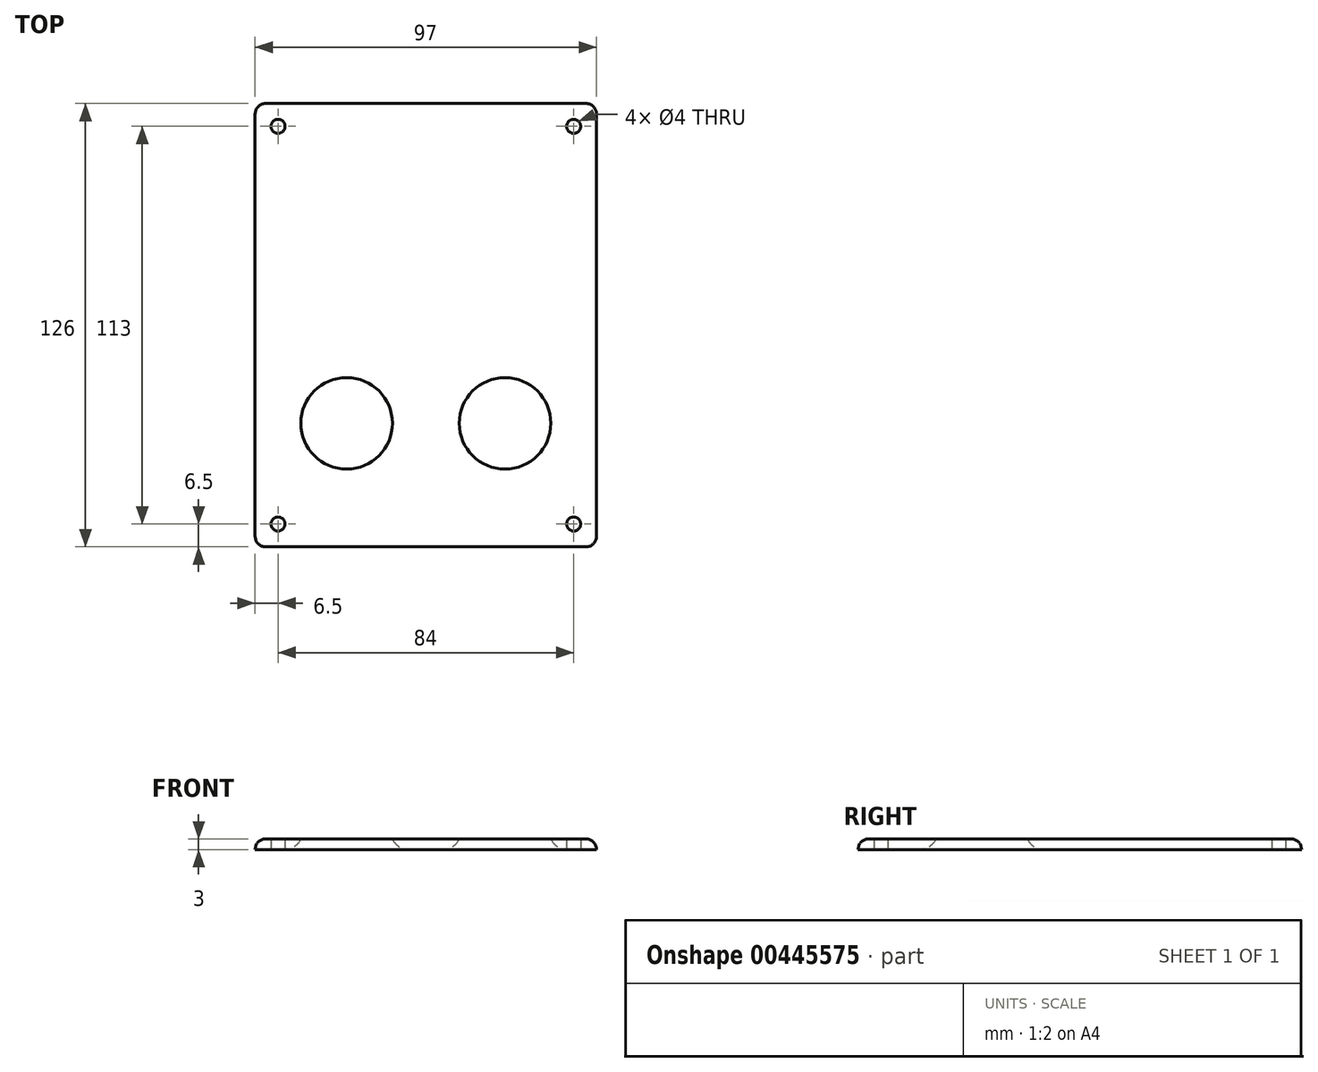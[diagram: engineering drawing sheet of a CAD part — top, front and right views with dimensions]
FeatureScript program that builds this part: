
annotation { "Feature Type Name" : "Feature", "Feature Type Description" : "" }
export const myFeature = defineFeature(function(context is Context, id is Id, definition is map)
    precondition{}
    {
        {
            var Q0;
            Q0=qCreatedBy(makeId("Top.planeOp"),FACE);
            var sketch = newSketch(context, id + "F0", { "sketchPlane" : qUnion([Q0])});
            skLineSegment(sketch, "E0.bottom", {"start": v(48.5, 63) * mm, "end": v(-48.5, 63) * mm});
            skLineSegment(sketch, "E0.top", {"start": v(48.5, -63) * mm, "end": v(-48.5, -63) * mm});
            skLineSegment(sketch, "E0.left", {"start": v(48.5, 63) * mm, "end": v(48.5, -63) * mm});
            skLineSegment(sketch, "E0.right", {"start": v(-48.5, 63) * mm, "end": v(-48.5, -63) * mm});
            skPoint(sketch, "E0.middle", {"position": v(0, 0) * mm});
            skLineSegment(sketch, "E1", {"start": v(-48.5, -27.89) * mm, "end": v(48.5, -27.88) * mm, "construction": true});
            skCircle(sketch, "E2", {"center": v(-22.5, -27.88) * mm, "radius": 13 * mm});
            skCircle(sketch, "E3", {"center": v(22.5, -27.88) * mm, "radius": 13 * mm});
            skLineSegment(sketch, "E4", {"start": v(-42, -63) * mm, "end": v(-42, 63) * mm, "construction": true});
            skLineSegment(sketch, "E5", {"start": v(0, -63) * mm, "end": v(0, 63) * mm, "construction": true});
            skLineSegment(sketch, "E6", {"start": v(-48.5, 56.5) * mm, "end": v(48.5, 56.5) * mm, "construction": true});
            skLineSegment(sketch, "E7", {"start": v(-48.5, 0) * mm, "end": v(48.5, 0) * mm, "construction": true});
            skCircle(sketch, "E8", {"center": v(-42, 56.5) * mm, "radius": 2 * mm});
            skCircle(sketch, "E9.MirrorC", {"center": v(42, 56.5) * mm, "radius": 2 * mm});
            skLineSegment(sketch, "E10.MirrorCS", {"start": v(48.5, 0) * mm, "end": v(-48.5, 0) * mm, "construction": true});
            skCircle(sketch, "E11.MirrorC", {"center": v(42, -56.5) * mm, "radius": 2 * mm});
            skCircle(sketch, "E12.MirrorC", {"center": v(-42, -56.5) * mm, "radius": 2 * mm});
            skLineSegment(sketch, "E13", {"start": v(-22.5, -63) * mm, "end": v(-22.5, 21.5) * mm, "construction": true});
            skLineSegment(sketch, "E14", {"start": v(22.5, -63) * mm, "end": v(22.5, 14.03) * mm, "construction": true});
            skSolve(sketch);
        }
        {
            var Q0;
            Q0=makeQuery(id+"F0.imprint","IMPRINT",FACE,{"disambiguationData":[TD([[makeQuery(id+"F0.imprint","IMPRINT",EDGE,{"derivedFrom":sQuery(id+"F0.wireOp",EDGE,"E0.bottom")}),1.0]])]});
            extrude(context, id + "F1", {"entities" : qUnion([Q0]), "depth" : 3 * mm});
        }
        {
            var Q0;
            Q0=makeQuery(id+"F1.opExtrude","CAP_EDGE",EDGE,{"disambiguationData":[OSD([sQuery(id+"F0.wireOp",EDGE,"E2")])],"isStart":true});
            fillet(context, id + "F2", {"entities" : qUnion([Q0]), "radius" : 5 * mm, "tangentPropagation" : true, "allowEdgeOverflow" : false});
        }
        {
            var Q0;
            Q0=makeQuery(id+"F1.opExtrude","CAP_EDGE",EDGE,{"disambiguationData":[OSD([sQuery(id+"F0.wireOp",EDGE,"E3")])],"isStart":true});
            fillet(context, id + "F3", {"entities" : qUnion([Q0]), "radius" : 5 * mm, "tangentPropagation" : true, "allowEdgeOverflow" : false});
        }
        {
            var Q0;
            Q0=makeQuery(id+"F1.opExtrude","SWEPT_EDGE",EDGE,{"disambiguationData":[OSD([sQuery(id+"F0.wireOp",EDGE,"E0.top"),sQuery(id+"F0.wireOp",EDGE,"E0.left")])]});
            var Q1;
            Q1=makeQuery(id+"F1.opExtrude","SWEPT_EDGE",EDGE,{"disambiguationData":[OSD([sQuery(id+"F0.wireOp",EDGE,"E0.top"),sQuery(id+"F0.wireOp",EDGE,"E0.right")])]});
            fillet(context, id + "F4", {"entities" : qUnion([Q0, Q1]), "radius" : 3 * mm, "tangentPropagation" : true, "allowEdgeOverflow" : false});
        }
        {
            var Q0;
            Q0=makeQuery(id+"F1.opExtrude","SWEPT_EDGE",EDGE,{"disambiguationData":[OSD([sQuery(id+"F0.wireOp",EDGE,"E0.bottom"),sQuery(id+"F0.wireOp",EDGE,"E0.left")])]});
            var Q1;
            Q1=makeQuery(id+"F1.opExtrude","SWEPT_EDGE",EDGE,{"disambiguationData":[OSD([sQuery(id+"F0.wireOp",EDGE,"E0.bottom"),sQuery(id+"F0.wireOp",EDGE,"E0.right")])]});
            fillet(context, id + "F5", {"entities" : qUnion([Q0, Q1]), "radius" : 3 * mm, "tangentPropagation" : true, "allowEdgeOverflow" : false});
        }
        {
            var Q0;
            Q0=makeQuery(id+"F1.opExtrude","CAP_EDGE",EDGE,{"disambiguationData":[OSD([sQuery(id+"F0.wireOp",EDGE,"E0.top")])],"isStart":false});
            var Q1;
            {var subQ0=sQuery(id+"F0.wireOp",EDGE,"E0.left");var subQ1=sQuery(id+"F0.wireOp",EDGE,"E0.top");Q1=makeQuery(id+"F4.opFillet","BLEND_EDGE",EDGE,{"blendedFrom":[makeQuery(id+"F1.opExtrude","SWEPT_EDGE",EDGE,{"disambiguationData":[OSD([subQ1,subQ0])]}),makeQuery(id+"F1.opExtrude","CAP_FACE",FACE,{"disambiguationData":[OSD([sQuery(id+"F0.wireOp",EDGE,"E0.bottom"),subQ1,subQ0,sQuery(id+"F0.wireOp",EDGE,"E0.right"),sQuery(id+"F0.wireOp",EDGE,"E2"),sQuery(id+"F0.wireOp",EDGE,"E3"),sQuery(id+"F0.wireOp",EDGE,"E8"),sQuery(id+"F0.wireOp",EDGE,"E9.MirrorC"),sQuery(id+"F0.wireOp",EDGE,"E11.MirrorC"),sQuery(id+"F0.wireOp",EDGE,"E12.MirrorC")])],"isStart":false})],"blendedInto":[makeQuery(id+"F1.opExtrude","CAP_FACE",FACE,{"disambiguationData":[OSD([sQuery(id+"F0.wireOp",EDGE,"E0.bottom"),subQ1,subQ0,sQuery(id+"F0.wireOp",EDGE,"E0.right"),sQuery(id+"F0.wireOp",EDGE,"E2"),sQuery(id+"F0.wireOp",EDGE,"E3"),sQuery(id+"F0.wireOp",EDGE,"E8"),sQuery(id+"F0.wireOp",EDGE,"E9.MirrorC"),sQuery(id+"F0.wireOp",EDGE,"E11.MirrorC"),sQuery(id+"F0.wireOp",EDGE,"E12.MirrorC")])],"isStart":false})]});}
            var Q2;
            Q2=makeQuery(id+"F1.opExtrude","CAP_EDGE",EDGE,{"disambiguationData":[OSD([sQuery(id+"F0.wireOp",EDGE,"E0.left")])],"isStart":false});
            var Q3;
            {var subQ0=sQuery(id+"F0.wireOp",EDGE,"E0.left");var subQ1=sQuery(id+"F0.wireOp",EDGE,"E0.bottom");Q3=makeQuery(id+"F5.opFillet","BLEND_EDGE",EDGE,{"blendedFrom":[makeQuery(id+"F1.opExtrude","SWEPT_EDGE",EDGE,{"disambiguationData":[OSD([subQ1,subQ0])]}),makeQuery(id+"F1.opExtrude","CAP_FACE",FACE,{"disambiguationData":[OSD([subQ1,sQuery(id+"F0.wireOp",EDGE,"E0.top"),subQ0,sQuery(id+"F0.wireOp",EDGE,"E0.right"),sQuery(id+"F0.wireOp",EDGE,"E2"),sQuery(id+"F0.wireOp",EDGE,"E3"),sQuery(id+"F0.wireOp",EDGE,"E8"),sQuery(id+"F0.wireOp",EDGE,"E9.MirrorC"),sQuery(id+"F0.wireOp",EDGE,"E11.MirrorC"),sQuery(id+"F0.wireOp",EDGE,"E12.MirrorC")])],"isStart":false})],"blendedInto":[makeQuery(id+"F1.opExtrude","CAP_FACE",FACE,{"disambiguationData":[OSD([subQ1,sQuery(id+"F0.wireOp",EDGE,"E0.top"),subQ0,sQuery(id+"F0.wireOp",EDGE,"E0.right"),sQuery(id+"F0.wireOp",EDGE,"E2"),sQuery(id+"F0.wireOp",EDGE,"E3"),sQuery(id+"F0.wireOp",EDGE,"E8"),sQuery(id+"F0.wireOp",EDGE,"E9.MirrorC"),sQuery(id+"F0.wireOp",EDGE,"E11.MirrorC"),sQuery(id+"F0.wireOp",EDGE,"E12.MirrorC")])],"isStart":false})]});}
            var Q4;
            Q4=makeQuery(id+"F1.opExtrude","CAP_EDGE",EDGE,{"disambiguationData":[OSD([sQuery(id+"F0.wireOp",EDGE,"E0.bottom")])],"isStart":false});
            var Q5;
            {var subQ0=sQuery(id+"F0.wireOp",EDGE,"E0.right");var subQ1=sQuery(id+"F0.wireOp",EDGE,"E0.bottom");Q5=makeQuery(id+"F5.opFillet","BLEND_EDGE",EDGE,{"blendedFrom":[makeQuery(id+"F1.opExtrude","SWEPT_EDGE",EDGE,{"disambiguationData":[OSD([subQ1,subQ0])]}),makeQuery(id+"F1.opExtrude","CAP_FACE",FACE,{"disambiguationData":[OSD([subQ1,sQuery(id+"F0.wireOp",EDGE,"E0.top"),sQuery(id+"F0.wireOp",EDGE,"E0.left"),subQ0,sQuery(id+"F0.wireOp",EDGE,"E2"),sQuery(id+"F0.wireOp",EDGE,"E3"),sQuery(id+"F0.wireOp",EDGE,"E8"),sQuery(id+"F0.wireOp",EDGE,"E9.MirrorC"),sQuery(id+"F0.wireOp",EDGE,"E11.MirrorC"),sQuery(id+"F0.wireOp",EDGE,"E12.MirrorC")])],"isStart":false})],"blendedInto":[makeQuery(id+"F1.opExtrude","CAP_FACE",FACE,{"disambiguationData":[OSD([subQ1,sQuery(id+"F0.wireOp",EDGE,"E0.top"),sQuery(id+"F0.wireOp",EDGE,"E0.left"),subQ0,sQuery(id+"F0.wireOp",EDGE,"E2"),sQuery(id+"F0.wireOp",EDGE,"E3"),sQuery(id+"F0.wireOp",EDGE,"E8"),sQuery(id+"F0.wireOp",EDGE,"E9.MirrorC"),sQuery(id+"F0.wireOp",EDGE,"E11.MirrorC"),sQuery(id+"F0.wireOp",EDGE,"E12.MirrorC")])],"isStart":false})]});}
            var Q6;
            Q6=makeQuery(id+"F1.opExtrude","CAP_EDGE",EDGE,{"disambiguationData":[OSD([sQuery(id+"F0.wireOp",EDGE,"E0.right")])],"isStart":false});
            var Q7;
            {var subQ0=sQuery(id+"F0.wireOp",EDGE,"E0.right");var subQ1=sQuery(id+"F0.wireOp",EDGE,"E0.top");Q7=makeQuery(id+"F4.opFillet","BLEND_EDGE",EDGE,{"blendedFrom":[makeQuery(id+"F1.opExtrude","SWEPT_EDGE",EDGE,{"disambiguationData":[OSD([subQ1,subQ0])]}),makeQuery(id+"F1.opExtrude","CAP_FACE",FACE,{"disambiguationData":[OSD([sQuery(id+"F0.wireOp",EDGE,"E0.bottom"),subQ1,sQuery(id+"F0.wireOp",EDGE,"E0.left"),subQ0,sQuery(id+"F0.wireOp",EDGE,"E2"),sQuery(id+"F0.wireOp",EDGE,"E3"),sQuery(id+"F0.wireOp",EDGE,"E8"),sQuery(id+"F0.wireOp",EDGE,"E9.MirrorC"),sQuery(id+"F0.wireOp",EDGE,"E11.MirrorC"),sQuery(id+"F0.wireOp",EDGE,"E12.MirrorC")])],"isStart":false})],"blendedInto":[makeQuery(id+"F1.opExtrude","CAP_FACE",FACE,{"disambiguationData":[OSD([sQuery(id+"F0.wireOp",EDGE,"E0.bottom"),subQ1,sQuery(id+"F0.wireOp",EDGE,"E0.left"),subQ0,sQuery(id+"F0.wireOp",EDGE,"E2"),sQuery(id+"F0.wireOp",EDGE,"E3"),sQuery(id+"F0.wireOp",EDGE,"E8"),sQuery(id+"F0.wireOp",EDGE,"E9.MirrorC"),sQuery(id+"F0.wireOp",EDGE,"E11.MirrorC"),sQuery(id+"F0.wireOp",EDGE,"E12.MirrorC")])],"isStart":false})]});}
            fillet(context, id + "F6", {"entities" : qUnion([Q0, Q1, Q2, Q3, Q4, Q5, Q6, Q7]), "radius" : 3 * mm, "tangentPropagation" : true, "allowEdgeOverflow" : false});
        }
    });
